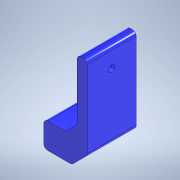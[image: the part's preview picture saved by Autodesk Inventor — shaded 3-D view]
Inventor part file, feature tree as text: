
AUTODESK INVENTOR PART (.ipt)
format: ipt  version: 2022 (Build 260153000, 153)  size: 165,376 bytes
history: native  units: mm
features: other x8, reference x6, sketch x4, extrude x3, chamfer x3, hole x1, fillet x1, projected_geometry x1
ambient origin geometry x8: Origin, YZ Plane, XZ Plane, XY Plane, X Axis, Y Axis, Z Axis, Center Point
bodies: Solid1 (feature_tree)
feature tree (27):
  extrude  "Extrusion1"  Depth=5.0mm
  extrude  "Extrusion2"  Depth=2.0mm
  extrude  "Extrusion3"  Depth=25.0mm
  chamfer  "Chamfer1"  Distance=25.0mm
  chamfer  "Chamfer3"  Distance=3.0mm
  hole  "Hole1"  [1 undecoded]
  fillet  "Fillet3"  Radius=2.0mm
  chamfer  "Chamfer4"  Distance=2.0mm Angle=45.0deg
  sketch  "Sketch1"  dims[d0=5.0mm d1=15.0mm]
  sketch  "Sketch2"  dims[d2=4.0mm d3=2.0mm]
  reference  "Reference1"
  reference  "Reference2"
  sketch  "Sketch3"  dims[d4=40.85mm d5=6.0mm d6=25.0mm d7=0.0mm]
  projected_geometry  "Projected Loop1"
  reference  "Reference3"
  reference  "Reference4"
  reference  "Reference5"
  sketch  "Sketch5"  dims[d8=7.0mm d9=3.0mm d10=0.0mm d13=3.0mm d14=0.0mm d16=7.75mm d17=2.0mm d18=45.0deg d24=6.0mm d25=2.0mm d26=45.0deg d27=3.4mm d28=6.0mm d29=6.5mm d30=3.4mm d31=90.0deg d32=8.0mm d33=20.594885mm d34=2.0mm d35=2.0mm d36=2.0mm d37=45.0deg d38=7.0mm]
  reference  "Reference6"
  parser-record x1  (decoder bookkeeping rows leaked as tree rows — omitted from the tree; the rows remain in map.json)
  other  "Bibble0.iam"
  other  "603 Bearing:10"
  other  "603 Bearing:14"
  other  "603 Bearing:15"
  other  "2020 Y Axis:5"
  other  "603 Bearing:12"
  other  "2020 X Axis:3"
note: 1 required parameter value undecoded (feature->parameter linkage not recoverable at this tier; creation-order binding heuristic only, values carry confidence <= 0.55)
note: 1 file-system path scrubbed to <path> (originals preserved in map.json)
